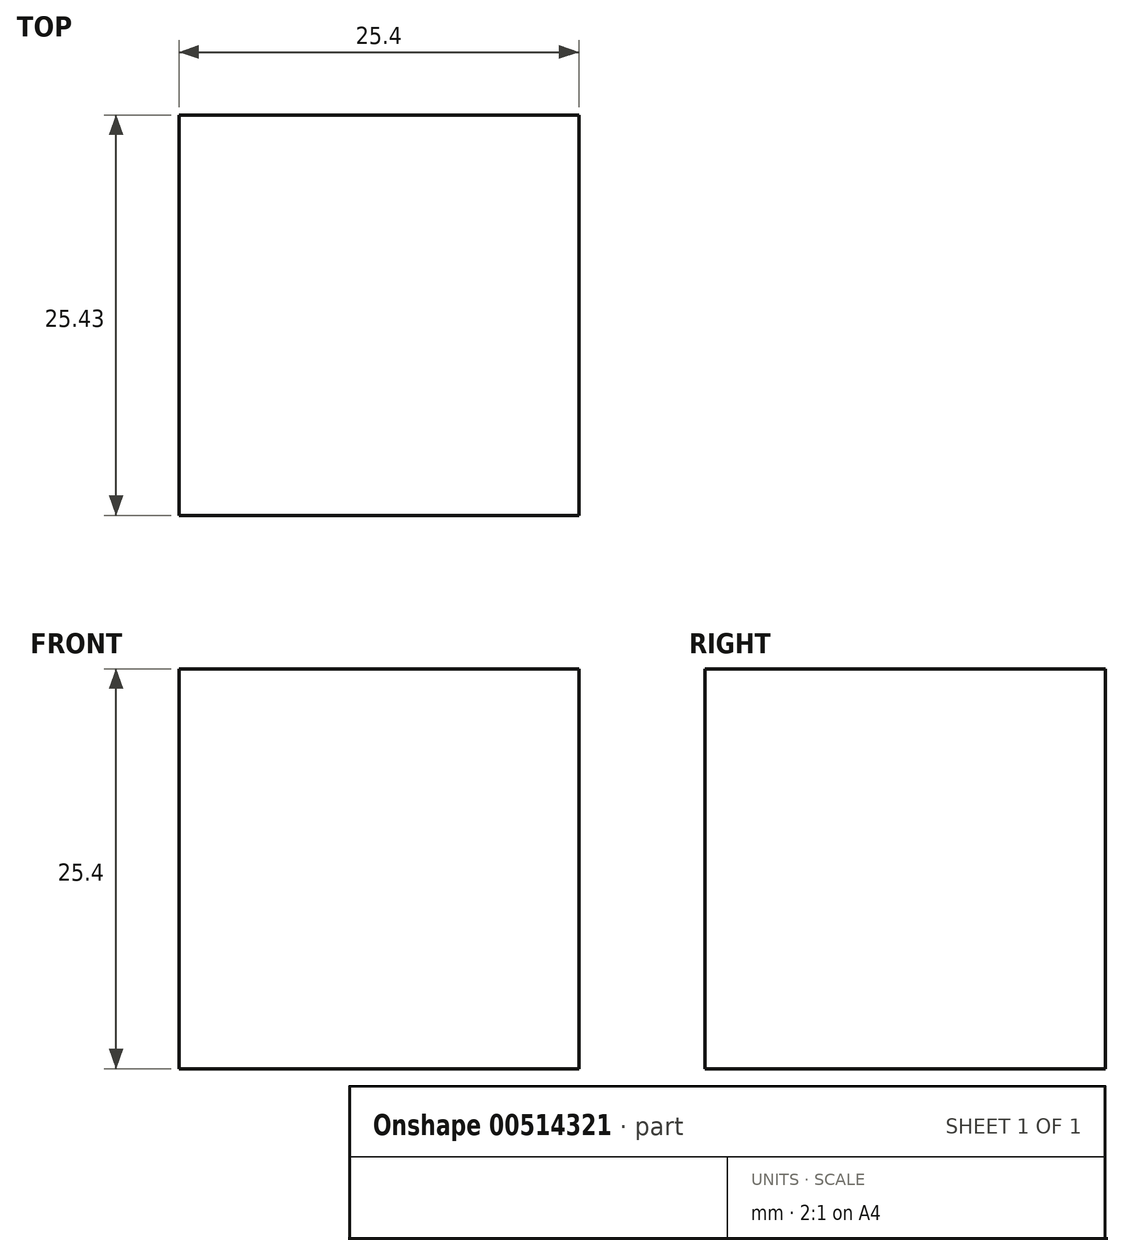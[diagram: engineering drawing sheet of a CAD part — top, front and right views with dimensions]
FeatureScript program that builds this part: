
annotation { "Feature Type Name" : "Feature", "Feature Type Description" : "" }
export const myFeature = defineFeature(function(context is Context, id is Id, definition is map)
    precondition{}
    {
        {
            var Q0;
            Q0=qCreatedBy(makeId("Top.planeOp"),FACE);
            var sketch = newSketch(context, id + "F0", { "sketchPlane" : qUnion([Q0])});
            skLineSegment(sketch, "E0.bottom", {"start": v(0, 0) * mm, "end": v(25.4, 0) * mm});
            skLineSegment(sketch, "E0.top", {"start": v(0, 25.43) * mm, "end": v(25.4, 25.43) * mm});
            skLineSegment(sketch, "E0.left", {"start": v(0, 0) * mm, "end": v(0, 25.43) * mm});
            skLineSegment(sketch, "E0.right", {"start": v(25.4, 0) * mm, "end": v(25.4, 25.43) * mm});
            skSolve(sketch);
        }
        {
            var Q0;
            Q0=makeQuery(id+"F0.imprint","IMPRINT",FACE,{"disambiguationData":[TD([[makeQuery(id+"F0.imprint","IMPRINT",EDGE,{"derivedFrom":sQuery(id+"F0.wireOp",EDGE,"E0.bottom")}),1.0]])]});
            extrude(context, id + "F1", {"entities" : qUnion([Q0]), "depth" : 25.4 * mm});
        }
    });
